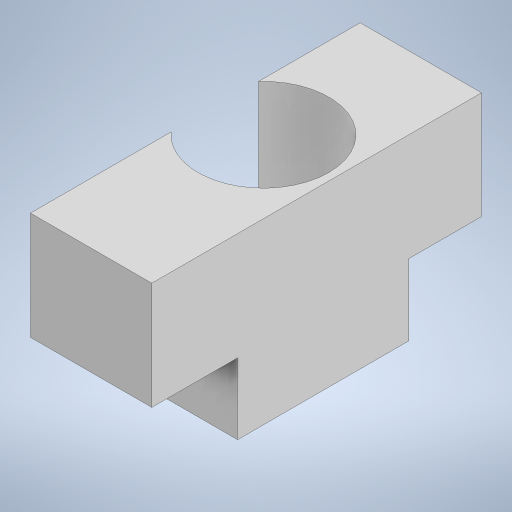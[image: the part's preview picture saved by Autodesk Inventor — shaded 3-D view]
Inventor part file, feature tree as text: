
AUTODESK INVENTOR PART (.ipt)
format: ipt  version: 2024.2 (Build 282272000, 272)  size: 306,688 bytes
history: native  units: in
note: dims shown in document units (in); Inventor stores cm internally (conversion verified against a paired STEP export)
features: extrude x11, sketch x11, projected_geometry x3
ambient origin geometry x8: Origin, YZ Plane, XZ Plane, XY Plane, X Axis, Y Axis, Z Axis, Center Point
bodies: Solid1 (feature_tree)
feature tree (25):
  extrude  "Extrusion1"  Depth=4.0in
  extrude  "Extrusion2"  Depth=0.1875in TaperAngle=0.0deg
  extrude  "Extrusion3"  TaperAngle=0.0deg  [1 undecoded]
  extrude  "Extrusion4"  Depth=1.0in
  extrude  "Extrusion5"  Depth=0.1875in
  extrude  "Extrusion6"  Depth=0.1875in
  extrude  "Extrusion7"  Depth=0.3937in TaperAngle=0.0deg
  extrude  "Extrusion8"  TaperAngle=0.0deg  [1 undecoded]
  extrude  "Extrusion9"  Depth=1.0in TaperAngle=0.0deg
  extrude  "Extrusion10"  Depth=0.6in TaperAngle=0.0deg
  extrude  "Extrusion11"  Depth=0.59in TaperAngle=0.0deg
  sketch  "Sketch1"  dims[d0=4.0in d1=4.0in]
  sketch  "Sketch2"  dims[d2=0.43in d3=0.1875in d4=0.0in]
  sketch  "Sketch3"  dims[d5=1.0in d6=0.0in]
  sketch  "Sketch4"  dims[d7=0.0in d8=0.0in d9=1.0in]
  sketch  "Sketch5"  dims[d10=0.16in d11=0.1875in]
  sketch  "Sketch6"  dims[d12=0.3149in d14=0.1875in]
  projected_geometry  "Projected Loop1"
  sketch  "Sketch7"  dims[d15=1.5748in d17=0.3936in d18=0.3937in d20=1.0in d22=1.0in d23=0.0in]
  sketch  "Sketch10"  dims[d24=0.075in d25=0.0in]
  sketch  "Sketch11"  dims[d26=0.311in d27=1.0in d28=0.0in]
  sketch  "Sketch12"  dims[d29=0.0in d30=0.0in d31=0.6in d32=0.0in]
  projected_geometry  "Projected Loop2"
  sketch  "Sketch13"  dims[d33=0.9in d34=0.59in d35=0.0in d36=0.5in d37=0.59in d38=0.0in d39=0.2in d40=0.59in d41=0.0in d42=0.1in d43=0.0in d44=0.54in d45=0.0in d13=0.0344in]
  projected_geometry  "Projected Loop3"
note: 2 required parameter values undecoded (feature->parameter linkage not recoverable at this tier; creation-order binding heuristic only, values carry confidence <= 0.55)
